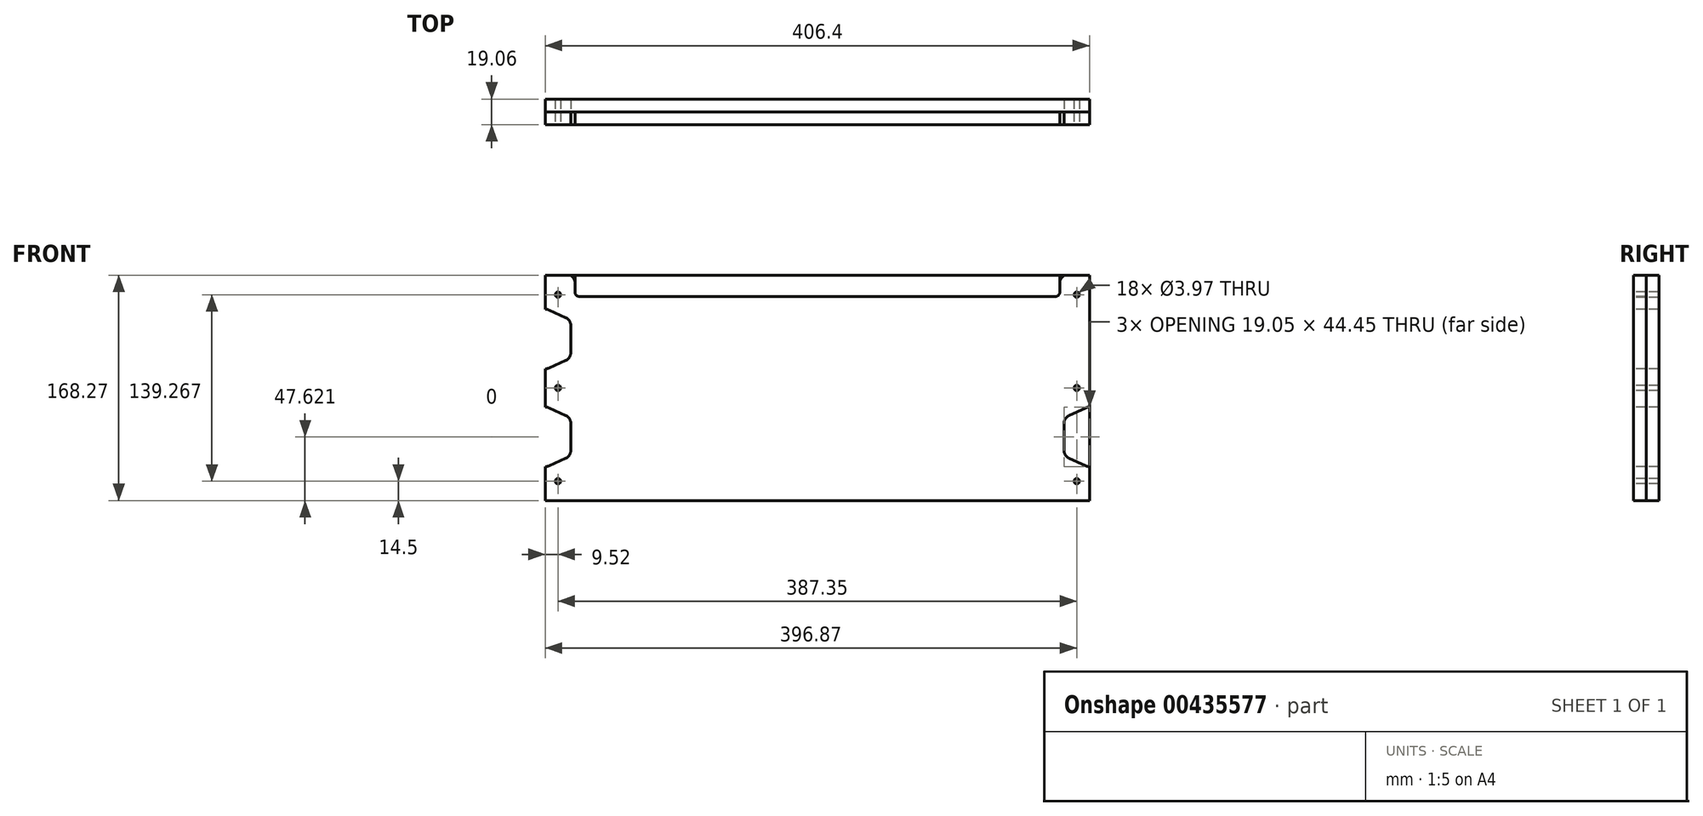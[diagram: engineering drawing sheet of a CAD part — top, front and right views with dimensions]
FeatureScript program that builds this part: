
annotation { "Feature Type Name" : "Feature", "Feature Type Description" : "" }
export const myFeature = defineFeature(function(context is Context, id is Id, definition is map)
    precondition{}
    {
        {
            var Q0;
            Q0=qCreatedBy(makeId("Front.planeOp"),FACE);
            var sketch = newSketch(context, id + "F0", { "sketchPlane" : qUnion([Q0])});
            skLineSegment(sketch, "E0", {"start": v(206.38, 21.72) * mm, "end": v(190.5, 21.72) * mm, "construction": true});
            skLineSegment(sketch, "E1", {"start": v(206.38, 25.32) * mm, "end": v(174.58, 10.87) * mm, "construction": true});
            skLineSegment(sketch, "E2", {"start": v(174.58, -11.9) * mm, "end": v(206.38, -26.34) * mm, "construction": true});
            skLineSegment(sketch, "E3", {"start": v(180.98, 21.72) * mm, "end": v(180.98, -29.08) * mm, "construction": true});
            skLineSegment(sketch, "E4", {"start": v(190.5, -22.73) * mm, "end": v(206.38, -22.73) * mm, "construction": true});
            skLineSegment(sketch, "E5", {"start": v(198.44, -35.43) * mm, "end": v(198.44, 28.07) * mm, "construction": true});
            skLineSegment(sketch, "E6", {"start": v(200.03, 28.07) * mm, "end": v(200.03, -35.43) * mm});
            skLineSegment(sketch, "E7", {"start": v(-184.15, 107.44) * mm, "end": v(-184.15, 120.14) * mm});
            skLineSegment(sketch, "E8", {"start": v(177.8, 107.44) * mm, "end": v(177.8, 120.14) * mm});
            skLineSegment(sketch, "E9", {"start": v(-180.97, 104.27) * mm, "end": v(174.63, 104.27) * mm});
            skLineSegment(sketch, "E10.bottom", {"start": v(-206.37, 120.14) * mm, "end": v(200.03, 120.14) * mm});
            skLineSegment(sketch, "E10.top", {"start": v(-206.37, -48.13) * mm, "end": v(200.03, -48.13) * mm});
            skLineSegment(sketch, "E10.left", {"start": v(-206.37, 120.14) * mm, "end": v(-206.37, -48.13) * mm});
            skLineSegment(sketch, "E10.right", {"start": v(200.03, 120.14) * mm, "end": v(200.03, -48.13) * mm});
            skLineSegment(sketch, "E11", {"start": v(-206.37, 36) * mm, "end": v(200.03, 36) * mm});
            skLineSegment(sketch, "E12", {"start": v(-3.17, 120.14) * mm, "end": v(-3.17, -48.13) * mm, "construction": true});
            skLineSegment(sketch, "E13", {"start": v(200.03, 21.72) * mm, "end": v(199.81, 21.72) * mm});
            skLineSegment(sketch, "E14", {"start": v(197.19, 21.15) * mm, "end": v(184.7, 15.47) * mm});
            skLineSegment(sketch, "E15", {"start": v(180.98, 9.69) * mm, "end": v(180.98, -10.7) * mm});
            skLineSegment(sketch, "E16", {"start": v(184.7, -16.49) * mm, "end": v(197.19, -22.16) * mm});
            skLineSegment(sketch, "E17", {"start": v(199.81, -22.73) * mm, "end": v(200.02, -22.73) * mm});
            skPoint(sketch, "E18.visualSharp", {"position": v(198.44, 21.72) * mm});
            skArc(sketch, "E18.filletArc", {"start": v(199.81, 21.72) * mm, "mid": v(198.47, 21.57) * mm, "end": v(197.19, 21.15) * mm});
            skPoint(sketch, "E19.visualSharp", {"position": v(180.98, 13.78) * mm});
            skArc(sketch, "E19.filletArc", {"start": v(184.7, 15.47) * mm, "mid": v(181.99, 13.13) * mm, "end": v(180.98, 9.69) * mm});
            skPoint(sketch, "E20.visualSharp", {"position": v(180.98, -14.8) * mm});
            skArc(sketch, "E20.filletArc", {"start": v(180.98, -10.7) * mm, "mid": v(181.99, -14.15) * mm, "end": v(184.7, -16.49) * mm});
            skPoint(sketch, "E21.visualSharp", {"position": v(198.44, -22.73) * mm});
            skArc(sketch, "E21.filletArc", {"start": v(197.19, -22.16) * mm, "mid": v(198.47, -22.59) * mm, "end": v(199.81, -22.73) * mm});
            skLineSegment(sketch, "E22.MirrorCS", {"start": v(-206.16, 94.74) * mm, "end": v(-206.37, 94.74) * mm});
            skArc(sketch, "E23.MirrorCS", {"start": v(-203.54, 94.17) * mm, "mid": v(-204.82, 94.6) * mm, "end": v(-206.16, 94.74) * mm});
            skArc(sketch, "E24.MirrorCS", {"start": v(-206.16, 50.3) * mm, "mid": v(-204.82, 50.44) * mm, "end": v(-203.54, 50.86) * mm});
            skLineSegment(sketch, "E25.MirrorCS", {"start": v(-206.38, 50.3) * mm, "end": v(-206.16, 50.3) * mm});
            skArc(sketch, "E26.MirrorCS", {"start": v(-191.05, 56.54) * mm, "mid": v(-188.34, 58.88) * mm, "end": v(-187.33, 62.32) * mm});
            skLineSegment(sketch, "E27.MirrorCS", {"start": v(-203.54, 50.86) * mm, "end": v(-191.05, 56.54) * mm});
            skLineSegment(sketch, "E28.MirrorCS", {"start": v(-187.33, 62.32) * mm, "end": v(-187.33, 82.71) * mm});
            skLineSegment(sketch, "E29.MirrorCS", {"start": v(-191.05, 88.5) * mm, "end": v(-203.54, 94.17) * mm});
            skArc(sketch, "E30.MirrorCS", {"start": v(-187.33, 82.71) * mm, "mid": v(-188.34, 86.15) * mm, "end": v(-191.05, 88.5) * mm});
            skLineSegment(sketch, "E31.MirrorCS", {"start": v(-206.38, 21.72) * mm, "end": v(-206.16, 21.72) * mm});
            skLineSegment(sketch, "E32.MirrorCS", {"start": v(-206.16, -22.73) * mm, "end": v(-206.37, -22.73) * mm});
            skArc(sketch, "E33.MirrorCS", {"start": v(-206.16, 21.72) * mm, "mid": v(-204.82, 21.57) * mm, "end": v(-203.54, 21.15) * mm});
            skArc(sketch, "E34.MirrorCS", {"start": v(-203.54, -22.16) * mm, "mid": v(-204.82, -22.59) * mm, "end": v(-206.16, -22.73) * mm});
            skLineSegment(sketch, "E35.MirrorCS", {"start": v(-187.33, 9.69) * mm, "end": v(-187.33, -10.7) * mm});
            skLineSegment(sketch, "E36.MirrorCS", {"start": v(-203.54, 21.15) * mm, "end": v(-191.05, 15.47) * mm});
            skArc(sketch, "E37.MirrorCS", {"start": v(-187.33, -10.7) * mm, "mid": v(-188.34, -14.15) * mm, "end": v(-191.05, -16.49) * mm});
            skLineSegment(sketch, "E38.MirrorCS", {"start": v(-191.05, -16.49) * mm, "end": v(-203.54, -22.16) * mm});
            skArc(sketch, "E39.MirrorCS", {"start": v(-191.05, 15.47) * mm, "mid": v(-188.34, 13.13) * mm, "end": v(-187.33, 9.69) * mm});
            skLineSegment(sketch, "E40.MirrorCS", {"start": v(200.03, 50.3) * mm, "end": v(199.81, 50.3) * mm});
            skLineSegment(sketch, "E41.MirrorCS", {"start": v(199.81, 94.74) * mm, "end": v(200.02, 94.74) * mm});
            skArc(sketch, "E42.MirrorCS", {"start": v(199.81, 50.3) * mm, "mid": v(198.47, 50.44) * mm, "end": v(197.19, 50.86) * mm});
            skArc(sketch, "E43.MirrorCS", {"start": v(197.19, 94.17) * mm, "mid": v(198.47, 94.6) * mm, "end": v(199.81, 94.74) * mm});
            skArc(sketch, "E44.MirrorCS", {"start": v(180.98, 82.71) * mm, "mid": v(181.99, 86.15) * mm, "end": v(184.7, 88.5) * mm});
            skArc(sketch, "E45.MirrorCS", {"start": v(184.7, 56.54) * mm, "mid": v(181.99, 58.88) * mm, "end": v(180.98, 62.32) * mm});
            skLineSegment(sketch, "E46.MirrorCS", {"start": v(190.5, 94.74) * mm, "end": v(206.38, 94.74) * mm, "construction": true});
            skLineSegment(sketch, "E47.MirrorCS", {"start": v(174.58, 83.9) * mm, "end": v(206.38, 98.35) * mm, "construction": true});
            skLineSegment(sketch, "E48.MirrorCS", {"start": v(206.38, 46.68) * mm, "end": v(174.58, 61.13) * mm, "construction": true});
            skLineSegment(sketch, "E49.MirrorCS", {"start": v(206.38, 50.3) * mm, "end": v(190.5, 50.3) * mm, "construction": true});
            skLineSegment(sketch, "E50.MirrorCS", {"start": v(180.98, 62.32) * mm, "end": v(180.98, 82.71) * mm});
            skLineSegment(sketch, "E51.MirrorCS", {"start": v(197.19, 50.86) * mm, "end": v(184.7, 56.54) * mm});
            skPoint(sketch, "E52.MirrorP", {"position": v(180.98, 58.23) * mm});
            skPoint(sketch, "E53.MirrorP", {"position": v(180.98, 86.8) * mm});
            skLineSegment(sketch, "E54.MirrorCS", {"start": v(184.7, 88.5) * mm, "end": v(197.19, 94.17) * mm});
            skPoint(sketch, "E55.MirrorP", {"position": v(198.44, 94.74) * mm});
            skLineSegment(sketch, "E56.MirrorCS", {"start": v(200.03, 47.12) * mm, "end": v(200.03, 110.62) * mm});
            skLineSegment(sketch, "E57.MirrorCS", {"start": v(180.98, 50.3) * mm, "end": v(180.98, 101.1) * mm, "construction": true});
            skLineSegment(sketch, "E58.MirrorCS", {"start": v(198.44, 107.44) * mm, "end": v(198.44, 43.94) * mm, "construction": true});
            skPoint(sketch, "E59.MirrorP", {"position": v(198.44, 50.3) * mm});
            skCircle(sketch, "E60", {"center": v(190.5, 105.64) * mm, "radius": 1.98 * mm});
            skCircle(sketch, "E61", {"center": v(190.5, 36) * mm, "radius": 1.98 * mm});
            skCircle(sketch, "E62.MirrorC", {"center": v(190.5, -33.63) * mm, "radius": 1.98 * mm});
            skCircle(sketch, "E63.MirrorC", {"center": v(-196.85, 105.64) * mm, "radius": 1.98 * mm});
            skCircle(sketch, "E64.MirrorC", {"center": v(-196.85, 36) * mm, "radius": 1.98 * mm});
            skCircle(sketch, "E65.MirrorC", {"center": v(-196.85, -33.63) * mm, "radius": 1.98 * mm});
            skPoint(sketch, "E66.visualSharp", {"position": v(-184.15, 104.27) * mm});
            skArc(sketch, "E66.filletArc", {"start": v(-184.15, 107.44) * mm, "mid": v(-183.22, 105.2) * mm, "end": v(-180.97, 104.27) * mm});
            skPoint(sketch, "E67.visualSharp", {"position": v(177.8, 104.27) * mm});
            skArc(sketch, "E67.filletArc", {"start": v(174.63, 104.27) * mm, "mid": v(176.87, 105.2) * mm, "end": v(177.8, 107.44) * mm});
            skSolve(sketch);
        }
        {
            var Q0;
            {var subQ15=sQuery(id+"F0.wireOp",EDGE,"E7");Q0=makeQuery(id+"F0.imprint","IMPRINT",FACE,{"disambiguationData":[TD([[makeQuery(id+"F0.imprint","IMPRINT",EDGE,{"derivedFrom":subQ15}),1.0]])]});}
            var Q1;
            {var subQ1=sQuery(id+"F0.wireOp",EDGE,"E10.top");Q1=makeQuery(id+"F0.imprint","IMPRINT",FACE,{"disambiguationData":[TD([[makeQuery(id+"F0.imprint","IMPRINT",EDGE,{"derivedFrom":subQ1}),1.0]])]});}
            var Q2;
            {var subQ0=sQuery(id+"F0.wireOp",EDGE,"E13");Q2=makeQuery(id+"F0.imprint","IMPRINT",FACE,{"disambiguationData":[TD([[makeQuery(id+"F0.imprint","IMPRINT",EDGE,{"derivedFrom":subQ0}),-1.0]])]});}
            var Q3;
            {var subQ0=sQuery(id+"F0.wireOp",EDGE,"E18.filletArc");var subQ3=sQuery(id+"F0.wireOp",EDGE,"E5");var subQ5=makeQuery(id+"F0.imprint","INTERSECT",VERTEX,{"derivedFrom":[subQ3,subQ0]});Q3=makeQuery(id+"F0.imprint","IMPRINT",FACE,{"disambiguationData":[TD([[makeQuery(id+"F0.imprint","IMPRINT",EDGE,{"disambiguationData":[TD([[subQ5,-1.0]])],"derivedFrom":subQ3}),-1.0]])]});}
            var Q4;
            {var subQ0=sQuery(id+"F0.wireOp",EDGE,"E1");var subQ1=makeQuery(id+"F0.imprint","IMPRINT",VERTEX,{"derivedFrom":subQ0});Q4=makeQuery(id+"F0.imprint","IMPRINT",FACE,{"disambiguationData":[TD([[makeQuery(id+"F0.imprint","IMPRINT",EDGE,{"disambiguationData":[TD([[subQ1,1.0]])],"derivedFrom":subQ0}),1.0]])]});}
            var Q5;
            {var subQ0=sQuery(id+"F0.wireOp",EDGE,"E19.filletArc");Q5=makeQuery(id+"F0.imprint","IMPRINT",FACE,{"disambiguationData":[TD([[makeQuery(id+"F0.imprint","IMPRINT",EDGE,{"derivedFrom":subQ0}),-1.0]])]});}
            var Q6;
            {var subQ0=sQuery(id+"F0.wireOp",EDGE,"E20.filletArc");Q6=makeQuery(id+"F0.imprint","IMPRINT",FACE,{"disambiguationData":[TD([[makeQuery(id+"F0.imprint","IMPRINT",EDGE,{"derivedFrom":subQ0}),-1.0]])]});}
            var Q7;
            {var subQ5=sQuery(id+"F0.wireOp",EDGE,"E17");Q7=makeQuery(id+"F0.imprint","IMPRINT",FACE,{"disambiguationData":[TD([[makeQuery(id+"F0.imprint","IMPRINT",EDGE,{"derivedFrom":subQ5}),-1.0]])]});}
            var Q8;
            {var subQ0=sQuery(id+"F0.wireOp",EDGE,"E21.filletArc");var subQ3=sQuery(id+"F0.wireOp",EDGE,"E5");var subQ5=makeQuery(id+"F0.imprint","INTERSECT",VERTEX,{"derivedFrom":[subQ3,subQ0]});Q8=makeQuery(id+"F0.imprint","IMPRINT",FACE,{"disambiguationData":[TD([[makeQuery(id+"F0.imprint","IMPRINT",EDGE,{"disambiguationData":[TD([[subQ5,1.0]])],"derivedFrom":subQ3}),-1.0]])]});}
            var Q9;
            {var subQ1=sQuery(id+"F0.wireOp",EDGE,"E2");var subQ3=sQuery(id+"F0.wireOp",EDGE,"E4");var subQ4=makeQuery(id+"F0.imprint","INTERSECT",VERTEX,{"derivedFrom":[subQ1,subQ3]});Q9=makeQuery(id+"F0.imprint","IMPRINT",FACE,{"disambiguationData":[TD([[makeQuery(id+"F0.imprint","IMPRINT",EDGE,{"disambiguationData":[TD([[subQ4,1.0]])],"derivedFrom":subQ1}),1.0]])]});}
            var Q10;
            {var subQ0=sQuery(id+"F0.wireOp",EDGE,"E46.MirrorCS");var subQ1=makeQuery(id+"F0.imprint","INTERSECT",VERTEX,{"derivedFrom":[sQuery(id+"F0.wireOp",EDGE,"E43.MirrorCS"),subQ0]});Q10=makeQuery(id+"F0.imprint","IMPRINT",FACE,{"disambiguationData":[TD([[makeQuery(id+"F0.imprint","IMPRINT",EDGE,{"disambiguationData":[TD([[subQ1,1.0]])],"derivedFrom":subQ0}),1.0]])]});}
            var Q11;
            {var subQ0=sQuery(id+"F0.wireOp",EDGE,"E56.MirrorCS");var subQ1=sQuery(id+"F0.wireOp",EDGE,"E48.MirrorCS");var subQ2=makeQuery(id+"F0.imprint","INTERSECT",VERTEX,{"derivedFrom":[subQ1,subQ0]});Q11=makeQuery(id+"F0.imprint","IMPRINT",FACE,{"disambiguationData":[TD([[makeQuery(id+"F0.imprint","IMPRINT",EDGE,{"disambiguationData":[TD([[subQ2,-1.0]])],"derivedFrom":subQ1}),-1.0]])]});}
            var Q12;
            {var subQ0=sQuery(id+"F0.wireOp",EDGE,"E47.MirrorCS");var subQ5=makeQuery(id+"F0.imprint","IMPRINT",VERTEX,{"derivedFrom":subQ0});Q12=makeQuery(id+"F0.imprint","IMPRINT",FACE,{"disambiguationData":[TD([[makeQuery(id+"F0.imprint","IMPRINT",EDGE,{"disambiguationData":[TD([[subQ5,1.0]])],"derivedFrom":subQ0}),-1.0]])]});}
            var Q13;
            {var subQ0=sQuery(id+"F0.wireOp",EDGE,"E46.MirrorCS");var subQ1=sQuery(id+"F0.wireOp",EDGE,"E43.MirrorCS");var subQ2=makeQuery(id+"F0.imprint","INTERSECT",VERTEX,{"derivedFrom":[subQ1,subQ0]});Q13=makeQuery(id+"F0.imprint","IMPRINT",FACE,{"disambiguationData":[TD([[makeQuery(id+"F0.imprint","IMPRINT",EDGE,{"disambiguationData":[TD([[subQ2,1.0]])],"derivedFrom":subQ1}),1.0]])]});}
            var Q14;
            {var subQ0=sQuery(id+"F0.wireOp",EDGE,"E44.MirrorCS");Q14=makeQuery(id+"F0.imprint","IMPRINT",FACE,{"disambiguationData":[TD([[makeQuery(id+"F0.imprint","IMPRINT",EDGE,{"derivedFrom":subQ0}),1.0]])]});}
            var Q15;
            {var subQ0=sQuery(id+"F0.wireOp",EDGE,"E45.MirrorCS");Q15=makeQuery(id+"F0.imprint","IMPRINT",FACE,{"disambiguationData":[TD([[makeQuery(id+"F0.imprint","IMPRINT",EDGE,{"derivedFrom":subQ0}),1.0]])]});}
            var Q16;
            {var subQ1=sQuery(id+"F0.wireOp",EDGE,"E42.MirrorCS");var subQ3=sQuery(id+"F0.wireOp",EDGE,"E58.MirrorCS");var subQ4=makeQuery(id+"F0.imprint","INTERSECT",VERTEX,{"derivedFrom":[subQ1,subQ3]});Q16=makeQuery(id+"F0.imprint","IMPRINT",FACE,{"disambiguationData":[TD([[makeQuery(id+"F0.imprint","IMPRINT",EDGE,{"disambiguationData":[TD([[subQ4,-1.0]])],"derivedFrom":subQ1}),1.0]])]});}
            var Q17;
            {var subQ0=sQuery(id+"F0.wireOp",EDGE,"E49.MirrorCS");var subQ1=sQuery(id+"F0.wireOp",EDGE,"E42.MirrorCS");var subQ2=makeQuery(id+"F0.imprint","INTERSECT",VERTEX,{"derivedFrom":[subQ1,subQ0]});Q17=makeQuery(id+"F0.imprint","IMPRINT",FACE,{"disambiguationData":[TD([[makeQuery(id+"F0.imprint","IMPRINT",EDGE,{"disambiguationData":[TD([[subQ2,-1.0]])],"derivedFrom":subQ1}),1.0]])]});}
            extrude(context, id + "F1", {"entities" : qUnion([Q0, Q1, Q2, Q3, Q4, Q5, Q6, Q7, Q8, Q9, Q10, Q11, Q12, Q13, Q14, Q15, Q16, Q17]), "depth" : 9.52 * mm});
        }
        {
            var Q0;
            {var subQ1=sQuery(id+"F0.wireOp",EDGE,"E10.top");Q0=makeQuery(id+"F0.imprint","IMPRINT",FACE,{"disambiguationData":[TD([[makeQuery(id+"F0.imprint","IMPRINT",EDGE,{"derivedFrom":subQ1}),1.0]])]});}
            var Q1;
            {var subQ15=sQuery(id+"F0.wireOp",EDGE,"E7");Q1=makeQuery(id+"F0.imprint","IMPRINT",FACE,{"disambiguationData":[TD([[makeQuery(id+"F0.imprint","IMPRINT",EDGE,{"derivedFrom":subQ15}),1.0]])]});}
            var Q2;
            {var subQ1=sQuery(id+"F0.wireOp",EDGE,"E7");Q2=makeQuery(id+"F0.imprint","IMPRINT",FACE,{"disambiguationData":[TD([[makeQuery(id+"F0.imprint","IMPRINT",EDGE,{"derivedFrom":subQ1}),-1.0]])]});}
            var Q3;
            {var subQ0=sQuery(id+"F0.wireOp",EDGE,"E20.filletArc");Q3=makeQuery(id+"F0.imprint","IMPRINT",FACE,{"disambiguationData":[TD([[makeQuery(id+"F0.imprint","IMPRINT",EDGE,{"derivedFrom":subQ0}),-1.0]])]});}
            var Q4;
            {var subQ5=sQuery(id+"F0.wireOp",EDGE,"E17");Q4=makeQuery(id+"F0.imprint","IMPRINT",FACE,{"disambiguationData":[TD([[makeQuery(id+"F0.imprint","IMPRINT",EDGE,{"derivedFrom":subQ5}),-1.0]])]});}
            var Q5;
            {var subQ0=sQuery(id+"F0.wireOp",EDGE,"E21.filletArc");var subQ3=sQuery(id+"F0.wireOp",EDGE,"E5");var subQ5=makeQuery(id+"F0.imprint","INTERSECT",VERTEX,{"derivedFrom":[subQ3,subQ0]});Q5=makeQuery(id+"F0.imprint","IMPRINT",FACE,{"disambiguationData":[TD([[makeQuery(id+"F0.imprint","IMPRINT",EDGE,{"disambiguationData":[TD([[subQ5,1.0]])],"derivedFrom":subQ3}),-1.0]])]});}
            var Q6;
            {var subQ1=sQuery(id+"F0.wireOp",EDGE,"E2");var subQ3=sQuery(id+"F0.wireOp",EDGE,"E4");var subQ4=makeQuery(id+"F0.imprint","INTERSECT",VERTEX,{"derivedFrom":[subQ1,subQ3]});Q6=makeQuery(id+"F0.imprint","IMPRINT",FACE,{"disambiguationData":[TD([[makeQuery(id+"F0.imprint","IMPRINT",EDGE,{"disambiguationData":[TD([[subQ4,1.0]])],"derivedFrom":subQ1}),1.0]])]});}
            var Q7;
            {var subQ0=sQuery(id+"F0.wireOp",EDGE,"E19.filletArc");Q7=makeQuery(id+"F0.imprint","IMPRINT",FACE,{"disambiguationData":[TD([[makeQuery(id+"F0.imprint","IMPRINT",EDGE,{"derivedFrom":subQ0}),-1.0]])]});}
            var Q8;
            {var subQ0=sQuery(id+"F0.wireOp",EDGE,"E1");var subQ1=makeQuery(id+"F0.imprint","IMPRINT",VERTEX,{"derivedFrom":subQ0});Q8=makeQuery(id+"F0.imprint","IMPRINT",FACE,{"disambiguationData":[TD([[makeQuery(id+"F0.imprint","IMPRINT",EDGE,{"disambiguationData":[TD([[subQ1,1.0]])],"derivedFrom":subQ0}),1.0]])]});}
            var Q9;
            {var subQ0=sQuery(id+"F0.wireOp",EDGE,"E18.filletArc");var subQ3=sQuery(id+"F0.wireOp",EDGE,"E5");var subQ5=makeQuery(id+"F0.imprint","INTERSECT",VERTEX,{"derivedFrom":[subQ3,subQ0]});Q9=makeQuery(id+"F0.imprint","IMPRINT",FACE,{"disambiguationData":[TD([[makeQuery(id+"F0.imprint","IMPRINT",EDGE,{"disambiguationData":[TD([[subQ5,-1.0]])],"derivedFrom":subQ3}),-1.0]])]});}
            var Q10;
            {var subQ0=sQuery(id+"F0.wireOp",EDGE,"E13");Q10=makeQuery(id+"F0.imprint","IMPRINT",FACE,{"disambiguationData":[TD([[makeQuery(id+"F0.imprint","IMPRINT",EDGE,{"derivedFrom":subQ0}),-1.0]])]});}
            var Q11;
            {var subQ0=sQuery(id+"F0.wireOp",EDGE,"E56.MirrorCS");var subQ1=sQuery(id+"F0.wireOp",EDGE,"E48.MirrorCS");var subQ2=makeQuery(id+"F0.imprint","INTERSECT",VERTEX,{"derivedFrom":[subQ1,subQ0]});Q11=makeQuery(id+"F0.imprint","IMPRINT",FACE,{"disambiguationData":[TD([[makeQuery(id+"F0.imprint","IMPRINT",EDGE,{"disambiguationData":[TD([[subQ2,-1.0]])],"derivedFrom":subQ1}),-1.0]])]});}
            var Q12;
            {var subQ0=sQuery(id+"F0.wireOp",EDGE,"E46.MirrorCS");var subQ1=makeQuery(id+"F0.imprint","INTERSECT",VERTEX,{"derivedFrom":[sQuery(id+"F0.wireOp",EDGE,"E43.MirrorCS"),subQ0]});Q12=makeQuery(id+"F0.imprint","IMPRINT",FACE,{"disambiguationData":[TD([[makeQuery(id+"F0.imprint","IMPRINT",EDGE,{"disambiguationData":[TD([[subQ1,1.0]])],"derivedFrom":subQ0}),1.0]])]});}
            var Q13;
            Q13=makeQuery(id+"F1.opExtrude","CAP_FACE",FACE,{"disambiguationData":[OSD([sQuery(id+"F0.wireOp",EDGE,"E6"),sQuery(id+"F0.wireOp",EDGE,"E7"),sQuery(id+"F0.wireOp",EDGE,"E8"),sQuery(id+"F0.wireOp",EDGE,"E9"),sQuery(id+"F0.wireOp",EDGE,"E10.bottom"),sQuery(id+"F0.wireOp",EDGE,"E10.top"),sQuery(id+"F0.wireOp",EDGE,"E10.right"),sQuery(id+"F0.wireOp",EDGE,"E13"),sQuery(id+"F0.wireOp",EDGE,"E14"),sQuery(id+"F0.wireOp",EDGE,"E15"),sQuery(id+"F0.wireOp",EDGE,"E16"),sQuery(id+"F0.wireOp",EDGE,"E17"),sQuery(id+"F0.wireOp",EDGE,"E18.filletArc"),sQuery(id+"F0.wireOp",EDGE,"E19.filletArc"),sQuery(id+"F0.wireOp",EDGE,"E20.filletArc"),sQuery(id+"F0.wireOp",EDGE,"E21.filletArc"),sQuery(id+"F0.wireOp",EDGE,"E22.MirrorCS"),sQuery(id+"F0.wireOp",EDGE,"E23.MirrorCS"),sQuery(id+"F0.wireOp",EDGE,"E24.MirrorCS"),sQuery(id+"F0.wireOp",EDGE,"E25.MirrorCS"),sQuery(id+"F0.wireOp",EDGE,"E26.MirrorCS"),sQuery(id+"F0.wireOp",EDGE,"E27.MirrorCS"),sQuery(id+"F0.wireOp",EDGE,"E28.MirrorCS"),sQuery(id+"F0.wireOp",EDGE,"E10.left"),sQuery(id+"F0.wireOp",EDGE,"E29.MirrorCS"),sQuery(id+"F0.wireOp",EDGE,"E30.MirrorCS"),sQuery(id+"F0.wireOp",EDGE,"E31.MirrorCS"),sQuery(id+"F0.wireOp",EDGE,"E32.MirrorCS"),sQuery(id+"F0.wireOp",EDGE,"E33.MirrorCS"),sQuery(id+"F0.wireOp",EDGE,"E34.MirrorCS"),sQuery(id+"F0.wireOp",EDGE,"E35.MirrorCS"),sQuery(id+"F0.wireOp",EDGE,"E36.MirrorCS"),sQuery(id+"F0.wireOp",EDGE,"E37.MirrorCS"),sQuery(id+"F0.wireOp",EDGE,"E38.MirrorCS"),sQuery(id+"F0.wireOp",EDGE,"E39.MirrorCS"),sQuery(id+"F0.wireOp",EDGE,"E42.MirrorCS"),sQuery(id+"F0.wireOp",EDGE,"E43.MirrorCS"),sQuery(id+"F0.wireOp",EDGE,"E44.MirrorCS"),sQuery(id+"F0.wireOp",EDGE,"E45.MirrorCS"),sQuery(id+"F0.wireOp",EDGE,"E46.MirrorCS"),sQuery(id+"F0.wireOp",EDGE,"E49.MirrorCS"),sQuery(id+"F0.wireOp",EDGE,"E51.MirrorCS"),sQuery(id+"F0.wireOp",EDGE,"E54.MirrorCS"),sQuery(id+"F0.wireOp",EDGE,"E56.MirrorCS"),sQuery(id+"F0.wireOp",EDGE,"E57.MirrorCS"),sQuery(id+"F0.wireOp",EDGE,"E60"),sQuery(id+"F0.wireOp",EDGE,"E61"),sQuery(id+"F0.wireOp",EDGE,"E62.MirrorC"),sQuery(id+"F0.wireOp",EDGE,"E63.MirrorC"),sQuery(id+"F0.wireOp",EDGE,"E64.MirrorC"),sQuery(id+"F0.wireOp",EDGE,"E65.MirrorC"),sQuery(id+"F0.wireOp",EDGE,"E66.filletArc"),sQuery(id+"F0.wireOp",EDGE,"E67.filletArc")])],"isStart":false});
            var Q14;
            {var subQ1=sQuery(id+"F0.wireOp",EDGE,"E42.MirrorCS");var subQ3=sQuery(id+"F0.wireOp",EDGE,"E58.MirrorCS");var subQ4=makeQuery(id+"F0.imprint","INTERSECT",VERTEX,{"derivedFrom":[subQ1,subQ3]});Q14=makeQuery(id+"F0.imprint","IMPRINT",FACE,{"disambiguationData":[TD([[makeQuery(id+"F0.imprint","IMPRINT",EDGE,{"disambiguationData":[TD([[subQ4,-1.0]])],"derivedFrom":subQ1}),1.0]])]});}
            var Q15;
            {var subQ0=sQuery(id+"F0.wireOp",EDGE,"E49.MirrorCS");var subQ1=sQuery(id+"F0.wireOp",EDGE,"E42.MirrorCS");var subQ2=makeQuery(id+"F0.imprint","INTERSECT",VERTEX,{"derivedFrom":[subQ1,subQ0]});Q15=makeQuery(id+"F0.imprint","IMPRINT",FACE,{"disambiguationData":[TD([[makeQuery(id+"F0.imprint","IMPRINT",EDGE,{"disambiguationData":[TD([[subQ2,-1.0]])],"derivedFrom":subQ1}),1.0]])]});}
            var Q16;
            {var subQ0=sQuery(id+"F0.wireOp",EDGE,"E45.MirrorCS");Q16=makeQuery(id+"F0.imprint","IMPRINT",FACE,{"disambiguationData":[TD([[makeQuery(id+"F0.imprint","IMPRINT",EDGE,{"derivedFrom":subQ0}),1.0]])]});}
            var Q17;
            {var subQ0=sQuery(id+"F0.wireOp",EDGE,"E44.MirrorCS");Q17=makeQuery(id+"F0.imprint","IMPRINT",FACE,{"disambiguationData":[TD([[makeQuery(id+"F0.imprint","IMPRINT",EDGE,{"derivedFrom":subQ0}),1.0]])]});}
            var Q18;
            {var subQ0=sQuery(id+"F0.wireOp",EDGE,"E47.MirrorCS");var subQ5=makeQuery(id+"F0.imprint","IMPRINT",VERTEX,{"derivedFrom":subQ0});Q18=makeQuery(id+"F0.imprint","IMPRINT",FACE,{"disambiguationData":[TD([[makeQuery(id+"F0.imprint","IMPRINT",EDGE,{"disambiguationData":[TD([[subQ5,1.0]])],"derivedFrom":subQ0}),-1.0]])]});}
            var Q19;
            {var subQ0=sQuery(id+"F0.wireOp",EDGE,"E46.MirrorCS");var subQ1=sQuery(id+"F0.wireOp",EDGE,"E43.MirrorCS");var subQ2=makeQuery(id+"F0.imprint","INTERSECT",VERTEX,{"derivedFrom":[subQ1,subQ0]});Q19=makeQuery(id+"F0.imprint","IMPRINT",FACE,{"disambiguationData":[TD([[makeQuery(id+"F0.imprint","IMPRINT",EDGE,{"disambiguationData":[TD([[subQ2,1.0]])],"derivedFrom":subQ1}),1.0]])]});}
            extrude(context, id + "F2", {"entities" : qUnion([Q0, Q1, Q2, Q3, Q4, Q5, Q6, Q7, Q8, Q9, Q10, Q11, Q12, Q13, Q14, Q15, Q16, Q17, Q18, Q19]), "operationType" : NewBodyOperationType.ADD, "oppositeDirection" : true, "depth" : 9.52 * mm});
        }
        {
            var Q0;
            Q0=makeQuery(id+"F1.opExtrude","SWEPT_EDGE",EDGE,{"disambiguationData":[OSD([sQuery(id+"F0.wireOp",EDGE,"E7"),sQuery(id+"F0.wireOp",EDGE,"E10.bottom")])]});
            var Q1;
            Q1=makeQuery(id+"F1.opExtrude","SWEPT_EDGE",EDGE,{"disambiguationData":[OSD([sQuery(id+"F0.wireOp",EDGE,"E8"),sQuery(id+"F0.wireOp",EDGE,"E10.bottom")])]});
            chamfer(context, id + "F3", {"entities" : qUnion([Q0, Q1]), "width" : 3.17 * mm, "tangentPropagation" : true});
        }
        {
            var Q0;
            {var subQ0=sQuery(id+"F0.wireOp",EDGE,"E7");Q0=makeQuery(id+"F3.opChamfer","BLEND_EDGE",EDGE,{"blendedFrom":[makeQuery(id+"F1.opExtrude","SWEPT_EDGE",EDGE,{"disambiguationData":[OSD([subQ0,sQuery(id+"F0.wireOp",EDGE,"E10.bottom")])]}),makeQuery(id+"F1.opExtrude","SWEPT_FACE",FACE,{"disambiguationData":[OSD([subQ0])]})],"blendedInto":[makeQuery(id+"F1.opExtrude","SWEPT_FACE",FACE,{"disambiguationData":[OSD([subQ0])]})]});}
            var Q1;
            {var subQ0=sQuery(id+"F0.wireOp",EDGE,"E8");Q1=makeQuery(id+"F3.opChamfer","BLEND_EDGE",EDGE,{"blendedFrom":[makeQuery(id+"F1.opExtrude","SWEPT_EDGE",EDGE,{"disambiguationData":[OSD([subQ0,sQuery(id+"F0.wireOp",EDGE,"E10.bottom")])]}),makeQuery(id+"F1.opExtrude","SWEPT_FACE",FACE,{"disambiguationData":[OSD([subQ0])]})],"blendedInto":[makeQuery(id+"F1.opExtrude","SWEPT_FACE",FACE,{"disambiguationData":[OSD([subQ0])]})]});}
            fillet(context, id + "F4", {"entities" : qUnion([Q0, Q1]), "radius" : 6.35 * mm, "tangentPropagation" : true, "allowEdgeOverflow" : false});
        }
    });
